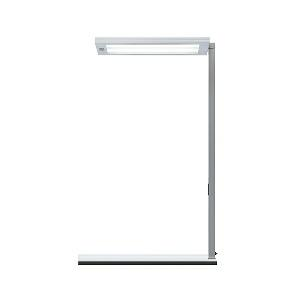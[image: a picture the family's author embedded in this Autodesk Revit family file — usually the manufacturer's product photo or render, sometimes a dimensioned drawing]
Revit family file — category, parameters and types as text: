
# Revit family: lavigo_-_dpt_9000_840_d_g2_00807254_e052
name_source: partatom
category: Lighting Fixtures
units: mm (PartAtom-declared; Revit-internal decimal feet)

## family parameters
Cut with Voids When Loaded = No
Host = Face
Light Source = No
Part Type = Normal
Room Calculation Point = No
Round Connector Dimension = Use Diameter
Shared = No

## types (1)
- LAVIGO - DPT 9000/840/D/G2 (1 x LED, 8950 lm, 4000K)
    Apparent Load = 63 VA
    Approval mark = CE
    CIE Flux Codes = 60 87 97 20 100
    Color Rendering = 80-89
    Color Temperature = 4000K
    Control Gear = Electronic ballast
    Default Elevation = 1800 mm
    Description = DPT 9000/840/D/G2|Desk-mounted luminaire|light source: LED|work equipment: Electronic ballast|connected load: 220-240 V, 50/60 Hz|Power consumption: approx. 63 W|standby: approx. 0,50|power factor: approx. 0,910|luminous flux: 8950 lm|luminous efficacy: 142 lm/W|light distribution: Direct/indirect|direct ratio: approx. 20 %|colour temperature: Cold white, ca. 4000 K|color rendering index (CRI): >= 80|chromaticity tolerance:  3 SDCM|technology: Continuously dimmable|operation: Multi-function switch|luminaire body|material: Steel/plastic|surface: Painted|colour: Silver metallic|lamp cover: Acrylic (PMMA), Satine|tubular section|material: Steel tube|surface: Painted|Form: Tubular section upright|colour of tubular section: Silver metallic|weight (net): approx. 9.5 kg|mains lead: 3.70 m Mains plug CEE 7/VII|Fastening: Socket, Table adaptor|decorative contrast side parts: Flint grey|glare control: Prism aperture|luminance(L65): <= 3000 cd/m|unified glare rating(4H 8H): <=  16|special features: Luminaire head detachable, Cradle to Cradle Certified TM, Direct light component with edge light and light-guide technology for homogenous light exit, Flicker-free, Inclination of tubular section adjustable, Separated, direct and indirect light individually adjustable|
    Frequency = 50 Hz, 60 Hz
    Height = 36 mm
    Lamp = 1 x LED
    Lamp Light Flux = 8950 lm
    Lamp count = 1
    Length = 675 mm
    Luminous efficacy = 142 lm/W
    Manufacturer = Waldmann
    ModVariant = No
    Model = 00807254
    Mounting Place = Table
    Mounting Type = Surface mounted
    Number of Poles = 1
    OnlyDefault = Yes
    Power Factor = 1
    Product Name = LAVIGO - DPT 9000/840/D/G2
    Product group = Desk mounted luminaire
    ProductGroupID = 22
    Protection Class = Protection class I
    Protection Degree = IP 20
    RLX_Detail_Level = 1
    RLX_Emergency_Light_Flux = 0 lm
    RLX_Emergency_Type = 0
    RLX_Emergency_Type_DB = No
    RlxData = <blob elided: 35301 chars, md5=1b2b1c1e>
    Socket = socket
    Standby Power = 0 W
    System Light Flux = 8950 lm
    System Power = 63 W
    Type Comments = Product without accessories
    Type Image = 121716000-00666945.jpg
    URL = http://relux.com
    VarID = ---
    Voltage = 230 V
    Voltage Range = 220-240 V
    Weight = 0.00 kg
    Width = 320 mm

## geometry (parser evidence)
native form markers: Blend x4, Sweep x15
no freeform markers — native parametric forms only
